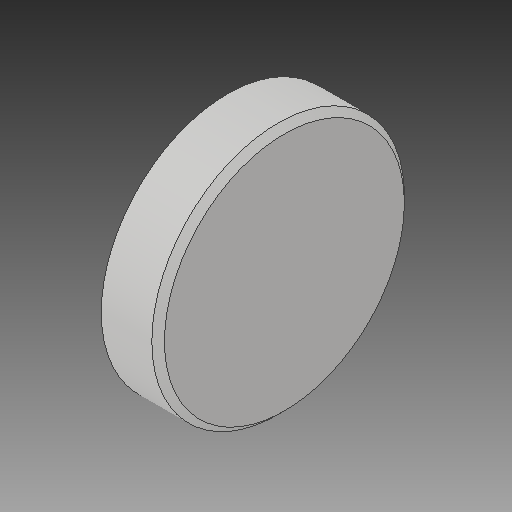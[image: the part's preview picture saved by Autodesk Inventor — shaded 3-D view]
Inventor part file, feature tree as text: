
AUTODESK INVENTOR PART (.ipt)
format: ipt  version: 2019 (Build 230136000, 136)  size: 94,208 bytes
history: native  units: in
note: dims shown in document units (in); Inventor stores cm internally (conversion verified against a paired STEP export)
features: chamfer x1
ambient origin geometry x8: Origin, YZ Plane, XZ Plane, XY Plane, X Axis, Y Axis, Z Axis, Center Point
bodies: Solid1 (feature_tree)
feature tree (1):
  chamfer  "Chamfer1"  [1 undecoded]
note: 1 required parameter value undecoded (feature->parameter linkage not recoverable at this tier; creation-order binding heuristic only, values carry confidence <= 0.55)
